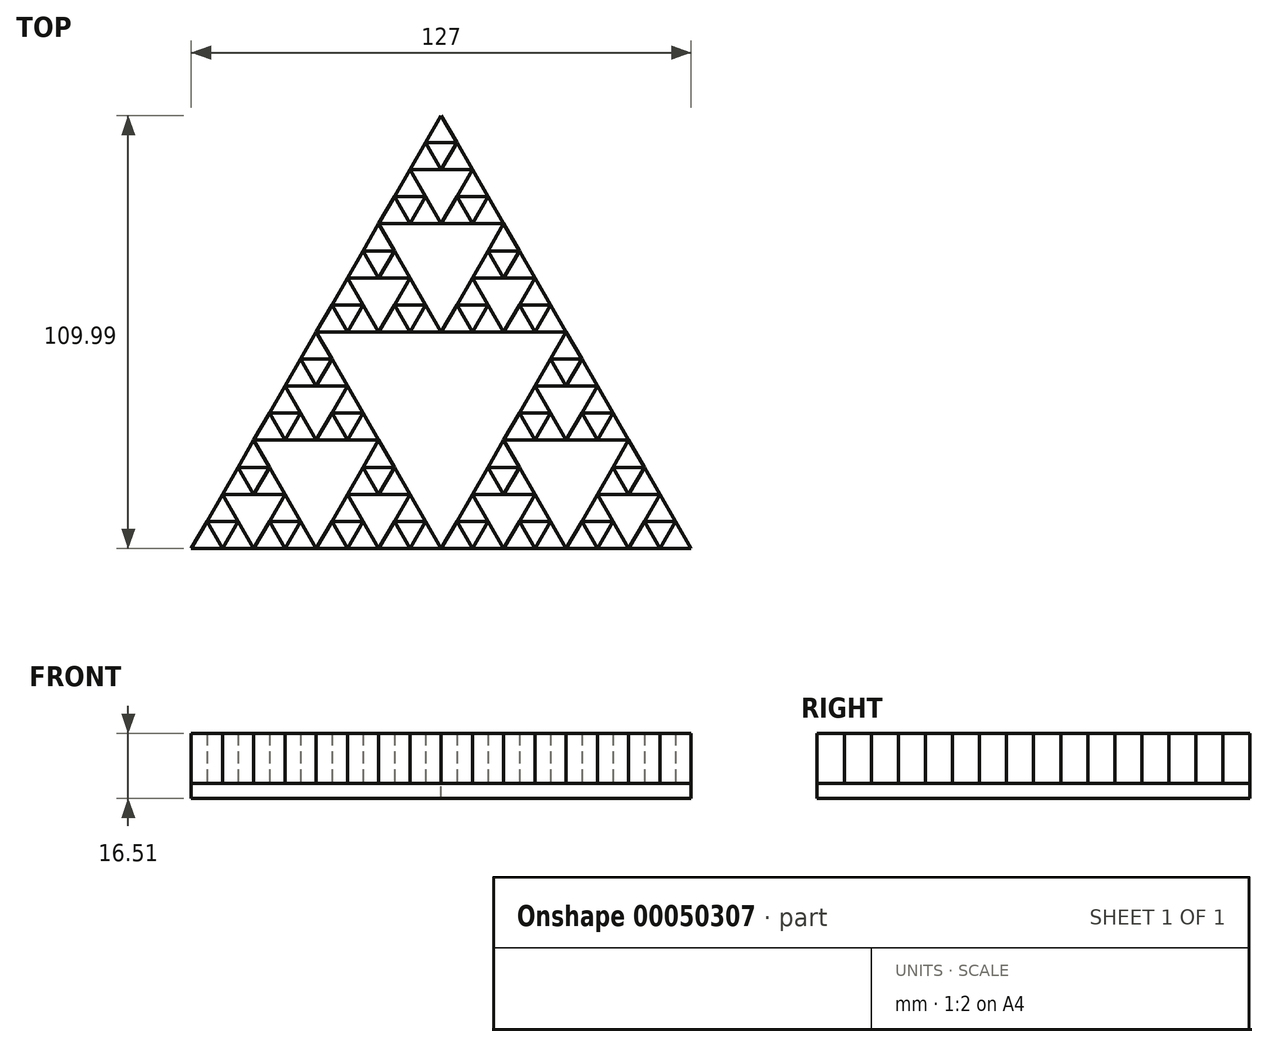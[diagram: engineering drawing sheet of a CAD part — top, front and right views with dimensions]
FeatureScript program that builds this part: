
annotation { "Feature Type Name" : "Feature", "Feature Type Description" : "" }
export const myFeature = defineFeature(function(context is Context, id is Id, definition is map)
    precondition{}
    {
        {
            var Q0;
            Q0=qCreatedBy(makeId("Top.planeOp"),FACE);
            var sketch = newSketch(context, id + "F0", { "sketchPlane" : qUnion([Q0])});
            skLineSegment(sketch, "E0", {"start": v(0, 109.99) * mm, "end": v(-63.5, 0) * mm});
            skLineSegment(sketch, "E1", {"start": v(-63.5, 0) * mm, "end": v(63.5, 0) * mm});
            skLineSegment(sketch, "E2", {"start": v(63.5, 0) * mm, "end": v(0, 109.99) * mm});
            skLineSegment(sketch, "E3", {"start": v(31.75, 55) * mm, "end": v(-31.75, 55) * mm});
            skLineSegment(sketch, "E4", {"start": v(-31.75, 55) * mm, "end": v(0, 0) * mm});
            skLineSegment(sketch, "E5", {"start": v(0, 0) * mm, "end": v(31.75, 55) * mm});
            skLineSegment(sketch, "E6", {"start": v(0, 55) * mm, "end": v(-15.88, 82.49) * mm});
            skLineSegment(sketch, "E7", {"start": v(-15.88, 82.49) * mm, "end": v(15.88, 82.49) * mm});
            skLineSegment(sketch, "E8", {"start": v(15.87, 82.49) * mm, "end": v(0, 55) * mm});
            skLineSegment(sketch, "E9", {"start": v(-15.88, 27.5) * mm, "end": v(-47.63, 27.5) * mm});
            skLineSegment(sketch, "E10", {"start": v(15.87, 27.5) * mm, "end": v(47.62, 27.5) * mm});
            skLineSegment(sketch, "E11", {"start": v(47.62, 27.5) * mm, "end": v(31.75, 0) * mm});
            skLineSegment(sketch, "E12", {"start": v(31.75, 0) * mm, "end": v(15.87, 27.5) * mm});
            skLineSegment(sketch, "E13", {"start": v(-15.88, 27.5) * mm, "end": v(-31.75, 0) * mm});
            skLineSegment(sketch, "E14", {"start": v(-31.75, 0) * mm, "end": v(-47.63, 27.5) * mm});
            skLineSegment(sketch, "E15", {"start": v(-31.75, 27.5) * mm, "end": v(-39.69, 41.24) * mm});
            skLineSegment(sketch, "E16", {"start": v(-39.69, 41.24) * mm, "end": v(-23.81, 41.24) * mm});
            skLineSegment(sketch, "E17", {"start": v(-23.81, 41.24) * mm, "end": v(-31.75, 27.5) * mm});
            skLineSegment(sketch, "E18", {"start": v(-23.81, 13.75) * mm, "end": v(-15.88, 0) * mm});
            skLineSegment(sketch, "E19", {"start": v(-15.88, 0) * mm, "end": v(-7.94, 13.75) * mm});
            skLineSegment(sketch, "E20", {"start": v(-7.94, 13.75) * mm, "end": v(-23.81, 13.75) * mm});
            skLineSegment(sketch, "E21", {"start": v(-39.69, 13.75) * mm, "end": v(-55.56, 13.75) * mm});
            skLineSegment(sketch, "E22", {"start": v(-39.69, 13.75) * mm, "end": v(-47.63, 0) * mm});
            skPoint(sketch, "E22.endSnap0", {"position": v(-47.63, 13.75) * mm});
            skLineSegment(sketch, "E23", {"start": v(-47.63, 0) * mm, "end": v(-55.56, 13.75) * mm});
            skLineSegment(sketch, "E24", {"start": v(23.81, 13.75) * mm, "end": v(15.87, 0) * mm});
            skLineSegment(sketch, "E25", {"start": v(15.87, 0) * mm, "end": v(7.94, 13.75) * mm});
            skLineSegment(sketch, "E26", {"start": v(7.94, 13.75) * mm, "end": v(23.81, 13.75) * mm});
            skLineSegment(sketch, "E27", {"start": v(39.69, 13.75) * mm, "end": v(55.56, 13.75) * mm});
            skLineSegment(sketch, "E28", {"start": v(55.56, 13.75) * mm, "end": v(47.62, 0) * mm});
            skPoint(sketch, "E28.endSnap0", {"position": v(47.62, 13.75) * mm});
            skLineSegment(sketch, "E29", {"start": v(47.62, 0) * mm, "end": v(39.69, 13.75) * mm});
            skLineSegment(sketch, "E30", {"start": v(31.75, 27.5) * mm, "end": v(23.81, 41.24) * mm});
            skLineSegment(sketch, "E31", {"start": v(23.81, 41.24) * mm, "end": v(39.69, 41.24) * mm});
            skLineSegment(sketch, "E32", {"start": v(39.69, 41.24) * mm, "end": v(31.75, 27.5) * mm});
            skLineSegment(sketch, "E33", {"start": v(7.94, 68.74) * mm, "end": v(15.87, 55) * mm});
            skLineSegment(sketch, "E34", {"start": v(15.87, 55) * mm, "end": v(23.81, 68.74) * mm});
            skLineSegment(sketch, "E35", {"start": v(23.81, 68.74) * mm, "end": v(7.94, 68.74) * mm});
            skLineSegment(sketch, "E36", {"start": v(-7.94, 68.74) * mm, "end": v(-15.88, 55) * mm});
            skLineSegment(sketch, "E37", {"start": v(-15.88, 55) * mm, "end": v(-23.81, 68.74) * mm});
            skLineSegment(sketch, "E38", {"start": v(-23.81, 68.74) * mm, "end": v(-7.94, 68.74) * mm});
            skLineSegment(sketch, "E39", {"start": v(0, 82.49) * mm, "end": v(-7.94, 96.24) * mm});
            skLineSegment(sketch, "E40", {"start": v(-7.94, 96.24) * mm, "end": v(7.94, 96.24) * mm});
            skLineSegment(sketch, "E41", {"start": v(7.94, 96.24) * mm, "end": v(0, 82.49) * mm});
            skLineSegment(sketch, "E42", {"start": v(0, 96.24) * mm, "end": v(3.97, 103.11) * mm});
            skLineSegment(sketch, "E43", {"start": v(3.97, 103.11) * mm, "end": v(-3.97, 103.11) * mm});
            skLineSegment(sketch, "E44", {"start": v(-3.97, 103.11) * mm, "end": v(0, 96.24) * mm});
            skLineSegment(sketch, "E45", {"start": v(-3.97, 89.36) * mm, "end": v(-11.9, 89.36) * mm});
            skLineSegment(sketch, "E46", {"start": v(-11.9, 89.36) * mm, "end": v(-7.94, 82.49) * mm});
            skLineSegment(sketch, "E47", {"start": v(-7.94, 82.49) * mm, "end": v(-3.97, 89.36) * mm});
            skLineSegment(sketch, "E48", {"start": v(3.97, 89.36) * mm, "end": v(11.9, 89.36) * mm});
            skLineSegment(sketch, "E49", {"start": v(11.9, 89.36) * mm, "end": v(7.94, 82.49) * mm});
            skLineSegment(sketch, "E50", {"start": v(7.94, 82.49) * mm, "end": v(3.97, 89.36) * mm});
            skLineSegment(sketch, "E51", {"start": v(-15.88, 68.74) * mm, "end": v(-19.84, 75.61) * mm});
            skLineSegment(sketch, "E52", {"start": v(-19.84, 75.61) * mm, "end": v(-11.9, 75.61) * mm});
            skLineSegment(sketch, "E53", {"start": v(-11.9, 75.61) * mm, "end": v(-15.88, 68.74) * mm});
            skLineSegment(sketch, "E54", {"start": v(-19.84, 61.87) * mm, "end": v(-27.78, 61.87) * mm});
            skLineSegment(sketch, "E55", {"start": v(-27.78, 61.87) * mm, "end": v(-23.81, 55) * mm});
            skLineSegment(sketch, "E56", {"start": v(-23.81, 55) * mm, "end": v(-19.84, 61.87) * mm});
            skLineSegment(sketch, "E57", {"start": v(-11.9, 61.87) * mm, "end": v(-3.97, 61.87) * mm});
            skPoint(sketch, "E57.endSnap0", {"position": v(-11.9, 61.87) * mm});
            skLineSegment(sketch, "E58", {"start": v(-3.97, 61.87) * mm, "end": v(-7.94, 55) * mm});
            skLineSegment(sketch, "E59", {"start": v(-7.94, 55) * mm, "end": v(-11.9, 61.87) * mm});
            skLineSegment(sketch, "E60", {"start": v(11.9, 61.87) * mm, "end": v(3.97, 61.87) * mm});
            skPoint(sketch, "E60.endSnap0", {"position": v(11.9, 61.87) * mm});
            skLineSegment(sketch, "E61", {"start": v(3.97, 61.87) * mm, "end": v(7.94, 55) * mm});
            skLineSegment(sketch, "E62", {"start": v(7.94, 55) * mm, "end": v(11.9, 61.87) * mm});
            skLineSegment(sketch, "E63", {"start": v(15.87, 68.74) * mm, "end": v(11.9, 75.61) * mm});
            skLineSegment(sketch, "E64", {"start": v(11.9, 75.61) * mm, "end": v(19.84, 75.61) * mm});
            skLineSegment(sketch, "E65", {"start": v(19.84, 75.61) * mm, "end": v(15.87, 68.74) * mm});
            skLineSegment(sketch, "E66", {"start": v(19.84, 61.87) * mm, "end": v(27.78, 61.87) * mm});
            skLineSegment(sketch, "E67", {"start": v(27.78, 61.87) * mm, "end": v(23.81, 55) * mm});
            skLineSegment(sketch, "E68", {"start": v(23.81, 55) * mm, "end": v(19.84, 61.87) * mm});
            skLineSegment(sketch, "E69", {"start": v(31.75, 41.24) * mm, "end": v(35.72, 48.12) * mm});
            skLineSegment(sketch, "E70", {"start": v(35.72, 48.12) * mm, "end": v(27.78, 48.12) * mm});
            skLineSegment(sketch, "E71", {"start": v(27.78, 48.12) * mm, "end": v(31.75, 41.24) * mm});
            skLineSegment(sketch, "E72", {"start": v(27.78, 34.37) * mm, "end": v(19.84, 34.37) * mm});
            skPoint(sketch, "E72.endSnap0", {"position": v(27.78, 34.37) * mm});
            skLineSegment(sketch, "E73", {"start": v(19.84, 34.37) * mm, "end": v(23.81, 27.5) * mm});
            skLineSegment(sketch, "E74", {"start": v(23.81, 27.5) * mm, "end": v(27.78, 34.37) * mm});
            skLineSegment(sketch, "E75", {"start": v(35.72, 34.37) * mm, "end": v(43.66, 34.37) * mm});
            skPoint(sketch, "E75.endSnap0", {"position": v(35.72, 34.37) * mm});
            skLineSegment(sketch, "E76", {"start": v(43.66, 34.37) * mm, "end": v(39.69, 27.5) * mm});
            skLineSegment(sketch, "E77", {"start": v(39.69, 27.5) * mm, "end": v(35.72, 34.37) * mm});
            skLineSegment(sketch, "E78", {"start": v(15.87, 13.75) * mm, "end": v(11.9, 20.62) * mm});
            skLineSegment(sketch, "E79", {"start": v(11.9, 20.62) * mm, "end": v(19.84, 20.62) * mm});
            skLineSegment(sketch, "E80", {"start": v(19.84, 20.62) * mm, "end": v(15.87, 13.75) * mm});
            skLineSegment(sketch, "E81", {"start": v(47.62, 13.75) * mm, "end": v(51.6, 20.62) * mm});
            skLineSegment(sketch, "E82", {"start": v(19.84, 6.87) * mm, "end": v(27.78, 6.87) * mm});
            skLineSegment(sketch, "E83", {"start": v(27.78, 6.87) * mm, "end": v(23.81, 0) * mm});
            skPoint(sketch, "E83.endSnap0", {"position": v(23.81, 6.87) * mm});
            skLineSegment(sketch, "E84", {"start": v(23.81, 0) * mm, "end": v(19.84, 6.87) * mm});
            skLineSegment(sketch, "E85", {"start": v(11.9, 6.87) * mm, "end": v(3.97, 6.87) * mm});
            skLineSegment(sketch, "E86", {"start": v(3.97, 6.87) * mm, "end": v(7.94, 0) * mm});
            skPoint(sketch, "E86.endSnap0", {"position": v(7.94, 6.87) * mm});
            skLineSegment(sketch, "E87", {"start": v(7.94, 0) * mm, "end": v(11.9, 6.87) * mm});
            skLineSegment(sketch, "E88", {"start": v(47.62, 13.75) * mm, "end": v(43.66, 20.62) * mm});
            skPoint(sketch, "E88.endSnap0", {"position": v(43.66, 6.87) * mm});
            skLineSegment(sketch, "E89", {"start": v(43.66, 20.62) * mm, "end": v(51.6, 20.62) * mm});
            skLineSegment(sketch, "E90", {"start": v(43.66, 6.87) * mm, "end": v(35.72, 6.87) * mm});
            skLineSegment(sketch, "E91", {"start": v(35.72, 6.87) * mm, "end": v(39.69, 0) * mm});
            skPoint(sketch, "E91.endSnap0", {"position": v(39.69, 6.87) * mm});
            skLineSegment(sketch, "E92", {"start": v(39.69, 0) * mm, "end": v(43.66, 6.87) * mm});
            skLineSegment(sketch, "E93", {"start": v(51.6, 6.87) * mm, "end": v(59.53, 6.87) * mm});
            skLineSegment(sketch, "E94", {"start": v(59.53, 6.87) * mm, "end": v(55.56, 0) * mm});
            skPoint(sketch, "E94.endSnap0", {"position": v(55.56, 6.87) * mm});
            skLineSegment(sketch, "E95", {"start": v(55.56, 0) * mm, "end": v(51.6, 6.87) * mm});
            skLineSegment(sketch, "E96", {"start": v(-31.75, 41.24) * mm, "end": v(-35.72, 48.12) * mm});
            skLineSegment(sketch, "E97", {"start": v(-35.72, 48.12) * mm, "end": v(-27.78, 48.12) * mm});
            skLineSegment(sketch, "E98", {"start": v(-27.78, 48.12) * mm, "end": v(-31.75, 41.24) * mm});
            skLineSegment(sketch, "E99", {"start": v(-35.72, 34.37) * mm, "end": v(-43.66, 34.37) * mm});
            skLineSegment(sketch, "E100", {"start": v(-43.66, 34.37) * mm, "end": v(-39.69, 27.5) * mm});
            skLineSegment(sketch, "E101", {"start": v(-39.69, 27.5) * mm, "end": v(-35.72, 34.37) * mm});
            skLineSegment(sketch, "E102", {"start": v(-27.78, 34.37) * mm, "end": v(-19.84, 34.37) * mm});
            skLineSegment(sketch, "E103", {"start": v(-19.84, 34.37) * mm, "end": v(-23.81, 27.5) * mm});
            skLineSegment(sketch, "E104", {"start": v(-23.81, 27.5) * mm, "end": v(-27.78, 34.37) * mm});
            skLineSegment(sketch, "E105", {"start": v(-47.63, 13.75) * mm, "end": v(-51.6, 20.62) * mm});
            skLineSegment(sketch, "E106", {"start": v(-51.6, 20.62) * mm, "end": v(-43.66, 20.62) * mm});
            skLineSegment(sketch, "E107", {"start": v(-43.66, 20.62) * mm, "end": v(-47.63, 13.75) * mm});
            skLineSegment(sketch, "E108", {"start": v(-15.88, 13.75) * mm, "end": v(-19.84, 20.62) * mm});
            skLineSegment(sketch, "E109", {"start": v(-19.84, 20.62) * mm, "end": v(-11.9, 20.62) * mm});
            skLineSegment(sketch, "E110", {"start": v(-11.9, 20.62) * mm, "end": v(-15.88, 13.75) * mm});
            skLineSegment(sketch, "E111", {"start": v(-19.84, 6.87) * mm, "end": v(-27.78, 6.87) * mm});
            skPoint(sketch, "E111.endSnap0", {"position": v(-19.84, 6.87) * mm});
            skLineSegment(sketch, "E112", {"start": v(-27.78, 6.87) * mm, "end": v(-23.81, 0) * mm});
            skPoint(sketch, "E112.endSnap0", {"position": v(-23.81, 6.87) * mm});
            skLineSegment(sketch, "E113", {"start": v(-23.81, 0) * mm, "end": v(-19.84, 6.87) * mm});
            skLineSegment(sketch, "E114", {"start": v(-43.66, 6.87) * mm, "end": v(-35.72, 6.87) * mm});
            skLineSegment(sketch, "E115", {"start": v(-35.72, 6.87) * mm, "end": v(-39.69, 0) * mm});
            skPoint(sketch, "E115.endSnap0", {"position": v(-39.69, 6.87) * mm});
            skLineSegment(sketch, "E116", {"start": v(-39.69, 0) * mm, "end": v(-43.66, 6.87) * mm});
            skLineSegment(sketch, "E117", {"start": v(-3.97, 6.87) * mm, "end": v(-11.9, 6.87) * mm});
            skPoint(sketch, "E117.startSnap0", {"position": v(-11.9, 6.87) * mm});
            skLineSegment(sketch, "E118", {"start": v(-11.9, 6.87) * mm, "end": v(-7.94, 0) * mm});
            skPoint(sketch, "E118.endSnap0", {"position": v(-7.94, 6.87) * mm});
            skLineSegment(sketch, "E119", {"start": v(-7.94, 0) * mm, "end": v(-3.97, 6.87) * mm});
            skLineSegment(sketch, "E120", {"start": v(-51.6, 6.87) * mm, "end": v(-59.53, 6.87) * mm});
            skLineSegment(sketch, "E121", {"start": v(-59.53, 6.87) * mm, "end": v(-55.56, 0) * mm});
            skPoint(sketch, "E121.endSnap0", {"position": v(-55.56, 6.87) * mm});
            skLineSegment(sketch, "E122", {"start": v(-55.56, 0) * mm, "end": v(-51.6, 6.87) * mm});
            skSolve(sketch);
        }
        {
            var Q0;
            {var subQ3=sQuery(id+"F0.wireOp",EDGE,"E43");Q0=makeQuery(id+"F0.imprint","IMPRINT",FACE,{"disambiguationData":[TD([[makeQuery(id+"F0.imprint","IMPRINT",EDGE,{"derivedFrom":subQ3}),-1.0]])]});}
            var Q1;
            {var subQ3=sQuery(id+"F0.wireOp",EDGE,"E44");Q1=makeQuery(id+"F0.imprint","IMPRINT",FACE,{"disambiguationData":[TD([[makeQuery(id+"F0.imprint","IMPRINT",EDGE,{"derivedFrom":subQ3}),-1.0]])]});}
            var Q2;
            {var subQ3=sQuery(id+"F0.wireOp",EDGE,"E42");Q2=makeQuery(id+"F0.imprint","IMPRINT",FACE,{"disambiguationData":[TD([[makeQuery(id+"F0.imprint","IMPRINT",EDGE,{"derivedFrom":subQ3}),-1.0]])]});}
            var Q3;
            {var subQ3=sQuery(id+"F0.wireOp",EDGE,"E48");Q3=makeQuery(id+"F0.imprint","IMPRINT",FACE,{"disambiguationData":[TD([[makeQuery(id+"F0.imprint","IMPRINT",EDGE,{"derivedFrom":subQ3}),1.0]])]});}
            var Q4;
            {var subQ3=sQuery(id+"F0.wireOp",EDGE,"E49");Q4=makeQuery(id+"F0.imprint","IMPRINT",FACE,{"disambiguationData":[TD([[makeQuery(id+"F0.imprint","IMPRINT",EDGE,{"derivedFrom":subQ3}),1.0]])]});}
            var Q5;
            {var subQ3=sQuery(id+"F0.wireOp",EDGE,"E50");Q5=makeQuery(id+"F0.imprint","IMPRINT",FACE,{"disambiguationData":[TD([[makeQuery(id+"F0.imprint","IMPRINT",EDGE,{"derivedFrom":subQ3}),1.0]])]});}
            var Q6;
            {var subQ3=sQuery(id+"F0.wireOp",EDGE,"E47");Q6=makeQuery(id+"F0.imprint","IMPRINT",FACE,{"disambiguationData":[TD([[makeQuery(id+"F0.imprint","IMPRINT",EDGE,{"derivedFrom":subQ3}),-1.0]])]});}
            var Q7;
            {var subQ3=sQuery(id+"F0.wireOp",EDGE,"E45");Q7=makeQuery(id+"F0.imprint","IMPRINT",FACE,{"disambiguationData":[TD([[makeQuery(id+"F0.imprint","IMPRINT",EDGE,{"derivedFrom":subQ3}),-1.0]])]});}
            var Q8;
            {var subQ3=sQuery(id+"F0.wireOp",EDGE,"E46");Q8=makeQuery(id+"F0.imprint","IMPRINT",FACE,{"disambiguationData":[TD([[makeQuery(id+"F0.imprint","IMPRINT",EDGE,{"derivedFrom":subQ3}),-1.0]])]});}
            var Q9;
            {var subQ3=sQuery(id+"F0.wireOp",EDGE,"E52");Q9=makeQuery(id+"F0.imprint","IMPRINT",FACE,{"disambiguationData":[TD([[makeQuery(id+"F0.imprint","IMPRINT",EDGE,{"derivedFrom":subQ3}),1.0]])]});}
            var Q10;
            {var subQ3=sQuery(id+"F0.wireOp",EDGE,"E51");Q10=makeQuery(id+"F0.imprint","IMPRINT",FACE,{"disambiguationData":[TD([[makeQuery(id+"F0.imprint","IMPRINT",EDGE,{"derivedFrom":subQ3}),1.0]])]});}
            var Q11;
            {var subQ3=sQuery(id+"F0.wireOp",EDGE,"E53");Q11=makeQuery(id+"F0.imprint","IMPRINT",FACE,{"disambiguationData":[TD([[makeQuery(id+"F0.imprint","IMPRINT",EDGE,{"derivedFrom":subQ3}),1.0]])]});}
            var Q12;
            {var subQ3=sQuery(id+"F0.wireOp",EDGE,"E64");Q12=makeQuery(id+"F0.imprint","IMPRINT",FACE,{"disambiguationData":[TD([[makeQuery(id+"F0.imprint","IMPRINT",EDGE,{"derivedFrom":subQ3}),1.0]])]});}
            var Q13;
            {var subQ3=sQuery(id+"F0.wireOp",EDGE,"E65");Q13=makeQuery(id+"F0.imprint","IMPRINT",FACE,{"disambiguationData":[TD([[makeQuery(id+"F0.imprint","IMPRINT",EDGE,{"derivedFrom":subQ3}),1.0]])]});}
            var Q14;
            {var subQ3=sQuery(id+"F0.wireOp",EDGE,"E63");Q14=makeQuery(id+"F0.imprint","IMPRINT",FACE,{"disambiguationData":[TD([[makeQuery(id+"F0.imprint","IMPRINT",EDGE,{"derivedFrom":subQ3}),1.0]])]});}
            var Q15;
            {var subQ3=sQuery(id+"F0.wireOp",EDGE,"E60");Q15=makeQuery(id+"F0.imprint","IMPRINT",FACE,{"disambiguationData":[TD([[makeQuery(id+"F0.imprint","IMPRINT",EDGE,{"derivedFrom":subQ3}),-1.0]])]});}
            var Q16;
            {var subQ3=sQuery(id+"F0.wireOp",EDGE,"E62");Q16=makeQuery(id+"F0.imprint","IMPRINT",FACE,{"disambiguationData":[TD([[makeQuery(id+"F0.imprint","IMPRINT",EDGE,{"derivedFrom":subQ3}),-1.0]])]});}
            var Q17;
            {var subQ3=sQuery(id+"F0.wireOp",EDGE,"E61");Q17=makeQuery(id+"F0.imprint","IMPRINT",FACE,{"disambiguationData":[TD([[makeQuery(id+"F0.imprint","IMPRINT",EDGE,{"derivedFrom":subQ3}),-1.0]])]});}
            var Q18;
            {var subQ3=sQuery(id+"F0.wireOp",EDGE,"E57");Q18=makeQuery(id+"F0.imprint","IMPRINT",FACE,{"disambiguationData":[TD([[makeQuery(id+"F0.imprint","IMPRINT",EDGE,{"derivedFrom":subQ3}),1.0]])]});}
            var Q19;
            {var subQ3=sQuery(id+"F0.wireOp",EDGE,"E58");Q19=makeQuery(id+"F0.imprint","IMPRINT",FACE,{"disambiguationData":[TD([[makeQuery(id+"F0.imprint","IMPRINT",EDGE,{"derivedFrom":subQ3}),1.0]])]});}
            var Q20;
            {var subQ3=sQuery(id+"F0.wireOp",EDGE,"E59");Q20=makeQuery(id+"F0.imprint","IMPRINT",FACE,{"disambiguationData":[TD([[makeQuery(id+"F0.imprint","IMPRINT",EDGE,{"derivedFrom":subQ3}),1.0]])]});}
            var Q21;
            {var subQ3=sQuery(id+"F0.wireOp",EDGE,"E56");Q21=makeQuery(id+"F0.imprint","IMPRINT",FACE,{"disambiguationData":[TD([[makeQuery(id+"F0.imprint","IMPRINT",EDGE,{"derivedFrom":subQ3}),-1.0]])]});}
            var Q22;
            {var subQ3=sQuery(id+"F0.wireOp",EDGE,"E54");Q22=makeQuery(id+"F0.imprint","IMPRINT",FACE,{"disambiguationData":[TD([[makeQuery(id+"F0.imprint","IMPRINT",EDGE,{"derivedFrom":subQ3}),-1.0]])]});}
            var Q23;
            {var subQ3=sQuery(id+"F0.wireOp",EDGE,"E55");Q23=makeQuery(id+"F0.imprint","IMPRINT",FACE,{"disambiguationData":[TD([[makeQuery(id+"F0.imprint","IMPRINT",EDGE,{"derivedFrom":subQ3}),-1.0]])]});}
            var Q24;
            {var subQ3=sQuery(id+"F0.wireOp",EDGE,"E66");Q24=makeQuery(id+"F0.imprint","IMPRINT",FACE,{"disambiguationData":[TD([[makeQuery(id+"F0.imprint","IMPRINT",EDGE,{"derivedFrom":subQ3}),1.0]])]});}
            var Q25;
            {var subQ3=sQuery(id+"F0.wireOp",EDGE,"E67");Q25=makeQuery(id+"F0.imprint","IMPRINT",FACE,{"disambiguationData":[TD([[makeQuery(id+"F0.imprint","IMPRINT",EDGE,{"derivedFrom":subQ3}),1.0]])]});}
            var Q26;
            {var subQ3=sQuery(id+"F0.wireOp",EDGE,"E68");Q26=makeQuery(id+"F0.imprint","IMPRINT",FACE,{"disambiguationData":[TD([[makeQuery(id+"F0.imprint","IMPRINT",EDGE,{"derivedFrom":subQ3}),1.0]])]});}
            var Q27;
            {var subQ3=sQuery(id+"F0.wireOp",EDGE,"E97");Q27=makeQuery(id+"F0.imprint","IMPRINT",FACE,{"disambiguationData":[TD([[makeQuery(id+"F0.imprint","IMPRINT",EDGE,{"derivedFrom":subQ3}),1.0]])]});}
            var Q28;
            {var subQ3=sQuery(id+"F0.wireOp",EDGE,"E96");Q28=makeQuery(id+"F0.imprint","IMPRINT",FACE,{"disambiguationData":[TD([[makeQuery(id+"F0.imprint","IMPRINT",EDGE,{"derivedFrom":subQ3}),1.0]])]});}
            var Q29;
            {var subQ3=sQuery(id+"F0.wireOp",EDGE,"E98");Q29=makeQuery(id+"F0.imprint","IMPRINT",FACE,{"disambiguationData":[TD([[makeQuery(id+"F0.imprint","IMPRINT",EDGE,{"derivedFrom":subQ3}),1.0]])]});}
            var Q30;
            {var subQ3=sQuery(id+"F0.wireOp",EDGE,"E102");Q30=makeQuery(id+"F0.imprint","IMPRINT",FACE,{"disambiguationData":[TD([[makeQuery(id+"F0.imprint","IMPRINT",EDGE,{"derivedFrom":subQ3}),1.0]])]});}
            var Q31;
            {var subQ3=sQuery(id+"F0.wireOp",EDGE,"E104");Q31=makeQuery(id+"F0.imprint","IMPRINT",FACE,{"disambiguationData":[TD([[makeQuery(id+"F0.imprint","IMPRINT",EDGE,{"derivedFrom":subQ3}),1.0]])]});}
            var Q32;
            {var subQ3=sQuery(id+"F0.wireOp",EDGE,"E103");Q32=makeQuery(id+"F0.imprint","IMPRINT",FACE,{"disambiguationData":[TD([[makeQuery(id+"F0.imprint","IMPRINT",EDGE,{"derivedFrom":subQ3}),1.0]])]});}
            var Q33;
            {var subQ3=sQuery(id+"F0.wireOp",EDGE,"E100");Q33=makeQuery(id+"F0.imprint","IMPRINT",FACE,{"disambiguationData":[TD([[makeQuery(id+"F0.imprint","IMPRINT",EDGE,{"derivedFrom":subQ3}),-1.0]])]});}
            var Q34;
            {var subQ3=sQuery(id+"F0.wireOp",EDGE,"E101");Q34=makeQuery(id+"F0.imprint","IMPRINT",FACE,{"disambiguationData":[TD([[makeQuery(id+"F0.imprint","IMPRINT",EDGE,{"derivedFrom":subQ3}),-1.0]])]});}
            var Q35;
            {var subQ3=sQuery(id+"F0.wireOp",EDGE,"E99");Q35=makeQuery(id+"F0.imprint","IMPRINT",FACE,{"disambiguationData":[TD([[makeQuery(id+"F0.imprint","IMPRINT",EDGE,{"derivedFrom":subQ3}),-1.0]])]});}
            var Q36;
            {var subQ3=sQuery(id+"F0.wireOp",EDGE,"E106");Q36=makeQuery(id+"F0.imprint","IMPRINT",FACE,{"disambiguationData":[TD([[makeQuery(id+"F0.imprint","IMPRINT",EDGE,{"derivedFrom":subQ3}),1.0]])]});}
            var Q37;
            {var subQ3=sQuery(id+"F0.wireOp",EDGE,"E105");Q37=makeQuery(id+"F0.imprint","IMPRINT",FACE,{"disambiguationData":[TD([[makeQuery(id+"F0.imprint","IMPRINT",EDGE,{"derivedFrom":subQ3}),1.0]])]});}
            var Q38;
            {var subQ3=sQuery(id+"F0.wireOp",EDGE,"E107");Q38=makeQuery(id+"F0.imprint","IMPRINT",FACE,{"disambiguationData":[TD([[makeQuery(id+"F0.imprint","IMPRINT",EDGE,{"derivedFrom":subQ3}),1.0]])]});}
            var Q39;
            {var subQ3=sQuery(id+"F0.wireOp",EDGE,"E114");Q39=makeQuery(id+"F0.imprint","IMPRINT",FACE,{"disambiguationData":[TD([[makeQuery(id+"F0.imprint","IMPRINT",EDGE,{"derivedFrom":subQ3}),1.0]])]});}
            var Q40;
            {var subQ3=sQuery(id+"F0.wireOp",EDGE,"E115");Q40=makeQuery(id+"F0.imprint","IMPRINT",FACE,{"disambiguationData":[TD([[makeQuery(id+"F0.imprint","IMPRINT",EDGE,{"derivedFrom":subQ3}),1.0]])]});}
            var Q41;
            {var subQ3=sQuery(id+"F0.wireOp",EDGE,"E116");Q41=makeQuery(id+"F0.imprint","IMPRINT",FACE,{"disambiguationData":[TD([[makeQuery(id+"F0.imprint","IMPRINT",EDGE,{"derivedFrom":subQ3}),1.0]])]});}
            var Q42;
            {var subQ3=sQuery(id+"F0.wireOp",EDGE,"E122");Q42=makeQuery(id+"F0.imprint","IMPRINT",FACE,{"disambiguationData":[TD([[makeQuery(id+"F0.imprint","IMPRINT",EDGE,{"derivedFrom":subQ3}),-1.0]])]});}
            var Q43;
            {var subQ3=sQuery(id+"F0.wireOp",EDGE,"E120");Q43=makeQuery(id+"F0.imprint","IMPRINT",FACE,{"disambiguationData":[TD([[makeQuery(id+"F0.imprint","IMPRINT",EDGE,{"derivedFrom":subQ3}),-1.0]])]});}
            var Q44;
            {var subQ3=sQuery(id+"F0.wireOp",EDGE,"E121");Q44=makeQuery(id+"F0.imprint","IMPRINT",FACE,{"disambiguationData":[TD([[makeQuery(id+"F0.imprint","IMPRINT",EDGE,{"derivedFrom":subQ3}),-1.0]])]});}
            var Q45;
            {var subQ3=sQuery(id+"F0.wireOp",EDGE,"E110");Q45=makeQuery(id+"F0.imprint","IMPRINT",FACE,{"disambiguationData":[TD([[makeQuery(id+"F0.imprint","IMPRINT",EDGE,{"derivedFrom":subQ3}),1.0]])]});}
            var Q46;
            {var subQ3=sQuery(id+"F0.wireOp",EDGE,"E108");Q46=makeQuery(id+"F0.imprint","IMPRINT",FACE,{"disambiguationData":[TD([[makeQuery(id+"F0.imprint","IMPRINT",EDGE,{"derivedFrom":subQ3}),1.0]])]});}
            var Q47;
            {var subQ3=sQuery(id+"F0.wireOp",EDGE,"E109");Q47=makeQuery(id+"F0.imprint","IMPRINT",FACE,{"disambiguationData":[TD([[makeQuery(id+"F0.imprint","IMPRINT",EDGE,{"derivedFrom":subQ3}),1.0]])]});}
            var Q48;
            {var subQ3=sQuery(id+"F0.wireOp",EDGE,"E117");Q48=makeQuery(id+"F0.imprint","IMPRINT",FACE,{"disambiguationData":[TD([[makeQuery(id+"F0.imprint","IMPRINT",EDGE,{"derivedFrom":subQ3}),-1.0]])]});}
            var Q49;
            {var subQ3=sQuery(id+"F0.wireOp",EDGE,"E119");Q49=makeQuery(id+"F0.imprint","IMPRINT",FACE,{"disambiguationData":[TD([[makeQuery(id+"F0.imprint","IMPRINT",EDGE,{"derivedFrom":subQ3}),-1.0]])]});}
            var Q50;
            {var subQ3=sQuery(id+"F0.wireOp",EDGE,"E118");Q50=makeQuery(id+"F0.imprint","IMPRINT",FACE,{"disambiguationData":[TD([[makeQuery(id+"F0.imprint","IMPRINT",EDGE,{"derivedFrom":subQ3}),-1.0]])]});}
            var Q51;
            {var subQ3=sQuery(id+"F0.wireOp",EDGE,"E113");Q51=makeQuery(id+"F0.imprint","IMPRINT",FACE,{"disambiguationData":[TD([[makeQuery(id+"F0.imprint","IMPRINT",EDGE,{"derivedFrom":subQ3}),-1.0]])]});}
            var Q52;
            {var subQ3=sQuery(id+"F0.wireOp",EDGE,"E111");Q52=makeQuery(id+"F0.imprint","IMPRINT",FACE,{"disambiguationData":[TD([[makeQuery(id+"F0.imprint","IMPRINT",EDGE,{"derivedFrom":subQ3}),-1.0]])]});}
            var Q53;
            {var subQ3=sQuery(id+"F0.wireOp",EDGE,"E112");Q53=makeQuery(id+"F0.imprint","IMPRINT",FACE,{"disambiguationData":[TD([[makeQuery(id+"F0.imprint","IMPRINT",EDGE,{"derivedFrom":subQ3}),-1.0]])]});}
            var Q54;
            {var subQ3=sQuery(id+"F0.wireOp",EDGE,"E70");Q54=makeQuery(id+"F0.imprint","IMPRINT",FACE,{"disambiguationData":[TD([[makeQuery(id+"F0.imprint","IMPRINT",EDGE,{"derivedFrom":subQ3}),-1.0]])]});}
            var Q55;
            {var subQ3=sQuery(id+"F0.wireOp",EDGE,"E69");Q55=makeQuery(id+"F0.imprint","IMPRINT",FACE,{"disambiguationData":[TD([[makeQuery(id+"F0.imprint","IMPRINT",EDGE,{"derivedFrom":subQ3}),-1.0]])]});}
            var Q56;
            {var subQ3=sQuery(id+"F0.wireOp",EDGE,"E71");Q56=makeQuery(id+"F0.imprint","IMPRINT",FACE,{"disambiguationData":[TD([[makeQuery(id+"F0.imprint","IMPRINT",EDGE,{"derivedFrom":subQ3}),-1.0]])]});}
            var Q57;
            {var subQ3=sQuery(id+"F0.wireOp",EDGE,"E72");Q57=makeQuery(id+"F0.imprint","IMPRINT",FACE,{"disambiguationData":[TD([[makeQuery(id+"F0.imprint","IMPRINT",EDGE,{"derivedFrom":subQ3}),-1.0]])]});}
            var Q58;
            {var subQ3=sQuery(id+"F0.wireOp",EDGE,"E74");Q58=makeQuery(id+"F0.imprint","IMPRINT",FACE,{"disambiguationData":[TD([[makeQuery(id+"F0.imprint","IMPRINT",EDGE,{"derivedFrom":subQ3}),-1.0]])]});}
            var Q59;
            {var subQ3=sQuery(id+"F0.wireOp",EDGE,"E73");Q59=makeQuery(id+"F0.imprint","IMPRINT",FACE,{"disambiguationData":[TD([[makeQuery(id+"F0.imprint","IMPRINT",EDGE,{"derivedFrom":subQ3}),-1.0]])]});}
            var Q60;
            {var subQ3=sQuery(id+"F0.wireOp",EDGE,"E79");Q60=makeQuery(id+"F0.imprint","IMPRINT",FACE,{"disambiguationData":[TD([[makeQuery(id+"F0.imprint","IMPRINT",EDGE,{"derivedFrom":subQ3}),1.0]])]});}
            var Q61;
            {var subQ3=sQuery(id+"F0.wireOp",EDGE,"E80");Q61=makeQuery(id+"F0.imprint","IMPRINT",FACE,{"disambiguationData":[TD([[makeQuery(id+"F0.imprint","IMPRINT",EDGE,{"derivedFrom":subQ3}),1.0]])]});}
            var Q62;
            {var subQ3=sQuery(id+"F0.wireOp",EDGE,"E78");Q62=makeQuery(id+"F0.imprint","IMPRINT",FACE,{"disambiguationData":[TD([[makeQuery(id+"F0.imprint","IMPRINT",EDGE,{"derivedFrom":subQ3}),1.0]])]});}
            var Q63;
            {var subQ3=sQuery(id+"F0.wireOp",EDGE,"E85");Q63=makeQuery(id+"F0.imprint","IMPRINT",FACE,{"disambiguationData":[TD([[makeQuery(id+"F0.imprint","IMPRINT",EDGE,{"derivedFrom":subQ3}),-1.0]])]});}
            var Q64;
            {var subQ3=sQuery(id+"F0.wireOp",EDGE,"E86");Q64=makeQuery(id+"F0.imprint","IMPRINT",FACE,{"disambiguationData":[TD([[makeQuery(id+"F0.imprint","IMPRINT",EDGE,{"derivedFrom":subQ3}),-1.0]])]});}
            var Q65;
            {var subQ3=sQuery(id+"F0.wireOp",EDGE,"E87");Q65=makeQuery(id+"F0.imprint","IMPRINT",FACE,{"disambiguationData":[TD([[makeQuery(id+"F0.imprint","IMPRINT",EDGE,{"derivedFrom":subQ3}),-1.0]])]});}
            var Q66;
            {var subQ3=sQuery(id+"F0.wireOp",EDGE,"E77");Q66=makeQuery(id+"F0.imprint","IMPRINT",FACE,{"disambiguationData":[TD([[makeQuery(id+"F0.imprint","IMPRINT",EDGE,{"derivedFrom":subQ3}),1.0]])]});}
            var Q67;
            {var subQ3=sQuery(id+"F0.wireOp",EDGE,"E75");Q67=makeQuery(id+"F0.imprint","IMPRINT",FACE,{"disambiguationData":[TD([[makeQuery(id+"F0.imprint","IMPRINT",EDGE,{"derivedFrom":subQ3}),1.0]])]});}
            var Q68;
            {var subQ3=sQuery(id+"F0.wireOp",EDGE,"E76");Q68=makeQuery(id+"F0.imprint","IMPRINT",FACE,{"disambiguationData":[TD([[makeQuery(id+"F0.imprint","IMPRINT",EDGE,{"derivedFrom":subQ3}),1.0]])]});}
            var Q69;
            {var subQ3=sQuery(id+"F0.wireOp",EDGE,"E89");Q69=makeQuery(id+"F0.imprint","IMPRINT",FACE,{"disambiguationData":[TD([[makeQuery(id+"F0.imprint","IMPRINT",EDGE,{"derivedFrom":subQ3}),1.0]])]});}
            var Q70;
            {var subQ3=sQuery(id+"F0.wireOp",EDGE,"E88");Q70=makeQuery(id+"F0.imprint","IMPRINT",FACE,{"disambiguationData":[TD([[makeQuery(id+"F0.imprint","IMPRINT",EDGE,{"derivedFrom":subQ3}),1.0]])]});}
            var Q71;
            {var subQ3=sQuery(id+"F0.wireOp",EDGE,"E81");Q71=makeQuery(id+"F0.imprint","IMPRINT",FACE,{"disambiguationData":[TD([[makeQuery(id+"F0.imprint","IMPRINT",EDGE,{"derivedFrom":subQ3}),-1.0]])]});}
            var Q72;
            {var subQ3=sQuery(id+"F0.wireOp",EDGE,"E93");Q72=makeQuery(id+"F0.imprint","IMPRINT",FACE,{"disambiguationData":[TD([[makeQuery(id+"F0.imprint","IMPRINT",EDGE,{"derivedFrom":subQ3}),1.0]])]});}
            var Q73;
            {var subQ3=sQuery(id+"F0.wireOp",EDGE,"E94");Q73=makeQuery(id+"F0.imprint","IMPRINT",FACE,{"disambiguationData":[TD([[makeQuery(id+"F0.imprint","IMPRINT",EDGE,{"derivedFrom":subQ3}),1.0]])]});}
            var Q74;
            {var subQ3=sQuery(id+"F0.wireOp",EDGE,"E95");Q74=makeQuery(id+"F0.imprint","IMPRINT",FACE,{"disambiguationData":[TD([[makeQuery(id+"F0.imprint","IMPRINT",EDGE,{"derivedFrom":subQ3}),1.0]])]});}
            var Q75;
            {var subQ3=sQuery(id+"F0.wireOp",EDGE,"E92");Q75=makeQuery(id+"F0.imprint","IMPRINT",FACE,{"disambiguationData":[TD([[makeQuery(id+"F0.imprint","IMPRINT",EDGE,{"derivedFrom":subQ3}),-1.0]])]});}
            var Q76;
            {var subQ3=sQuery(id+"F0.wireOp",EDGE,"E90");Q76=makeQuery(id+"F0.imprint","IMPRINT",FACE,{"disambiguationData":[TD([[makeQuery(id+"F0.imprint","IMPRINT",EDGE,{"derivedFrom":subQ3}),-1.0]])]});}
            var Q77;
            {var subQ3=sQuery(id+"F0.wireOp",EDGE,"E91");Q77=makeQuery(id+"F0.imprint","IMPRINT",FACE,{"disambiguationData":[TD([[makeQuery(id+"F0.imprint","IMPRINT",EDGE,{"derivedFrom":subQ3}),-1.0]])]});}
            var Q78;
            {var subQ3=sQuery(id+"F0.wireOp",EDGE,"E83");Q78=makeQuery(id+"F0.imprint","IMPRINT",FACE,{"disambiguationData":[TD([[makeQuery(id+"F0.imprint","IMPRINT",EDGE,{"derivedFrom":subQ3}),1.0]])]});}
            var Q79;
            {var subQ3=sQuery(id+"F0.wireOp",EDGE,"E82");Q79=makeQuery(id+"F0.imprint","IMPRINT",FACE,{"disambiguationData":[TD([[makeQuery(id+"F0.imprint","IMPRINT",EDGE,{"derivedFrom":subQ3}),1.0]])]});}
            var Q80;
            {var subQ3=sQuery(id+"F0.wireOp",EDGE,"E84");Q80=makeQuery(id+"F0.imprint","IMPRINT",FACE,{"disambiguationData":[TD([[makeQuery(id+"F0.imprint","IMPRINT",EDGE,{"derivedFrom":subQ3}),1.0]])]});}
            extrude(context, id + "F1", {"entities" : qUnion([Q0, Q1, Q2, Q3, Q4, Q5, Q6, Q7, Q8, Q9, Q10, Q11, Q12, Q13, Q14, Q15, Q16, Q17, Q18, Q19, Q20, Q21, Q22, Q23, Q24, Q25, Q26, Q27, Q28, Q29, Q30, Q31, Q32, Q33, Q34, Q35, Q36, Q37, Q38, Q39, Q40, Q41, Q42, Q43, Q44, Q45, Q46, Q47, Q48, Q49, Q50, Q51, Q52, Q53, Q54, Q55, Q56, Q57, Q58, Q59, Q60, Q61, Q62, Q63, Q64, Q65, Q66, Q67, Q68, Q69, Q70, Q71, Q72, Q73, Q74, Q75, Q76, Q77, Q78, Q79, Q80]), "depth" : 12.7 * mm});
        }
        {
            var Q0;
            {var subQ3=sQuery(id+"F0.wireOp",EDGE,"E43");Q0=makeQuery(id+"F0.imprint","IMPRINT",FACE,{"disambiguationData":[TD([[makeQuery(id+"F0.imprint","IMPRINT",EDGE,{"derivedFrom":subQ3}),-1.0]])]});}
            var Q1;
            Q1=makeQuery(id+"F0.imprint","IMPRINT",FACE,{"disambiguationData":[TD([[makeQuery(id+"F0.imprint","IMPRINT",EDGE,{"derivedFrom":sQuery(id+"F0.wireOp",EDGE,"E42")}),1.0]])]});
            var Q2;
            {var subQ3=sQuery(id+"F0.wireOp",EDGE,"E42");Q2=makeQuery(id+"F0.imprint","IMPRINT",FACE,{"disambiguationData":[TD([[makeQuery(id+"F0.imprint","IMPRINT",EDGE,{"derivedFrom":subQ3}),-1.0]])]});}
            var Q3;
            {var subQ3=sQuery(id+"F0.wireOp",EDGE,"E44");Q3=makeQuery(id+"F0.imprint","IMPRINT",FACE,{"disambiguationData":[TD([[makeQuery(id+"F0.imprint","IMPRINT",EDGE,{"derivedFrom":subQ3}),-1.0]])]});}
            var Q4;
            {var subQ3=sQuery(id+"F0.wireOp",EDGE,"E48");Q4=makeQuery(id+"F0.imprint","IMPRINT",FACE,{"disambiguationData":[TD([[makeQuery(id+"F0.imprint","IMPRINT",EDGE,{"derivedFrom":subQ3}),1.0]])]});}
            var Q5;
            {var subQ0=sQuery(id+"F0.wireOp",EDGE,"E41");var subQ4=sQuery(id+"F0.wireOp",EDGE,"E39");var subQ7=makeQuery(id+"F0.imprint","INTERSECT",VERTEX,{"derivedFrom":[sQuery(id+"F0.wireOp",EDGE,"E7"),subQ4,subQ0]});Q5=makeQuery(id+"F0.imprint","IMPRINT",FACE,{"disambiguationData":[TD([[makeQuery(id+"F0.imprint","IMPRINT",EDGE,{"disambiguationData":[TD([[subQ7,-1.0]])],"derivedFrom":subQ4}),-1.0]])]});}
            var Q6;
            Q6=makeQuery(id+"F0.imprint","IMPRINT",FACE,{"disambiguationData":[TD([[makeQuery(id+"F0.imprint","IMPRINT",EDGE,{"derivedFrom":sQuery(id+"F0.wireOp",EDGE,"E48")}),-1.0]])]});
            var Q7;
            {var subQ3=sQuery(id+"F0.wireOp",EDGE,"E49");Q7=makeQuery(id+"F0.imprint","IMPRINT",FACE,{"disambiguationData":[TD([[makeQuery(id+"F0.imprint","IMPRINT",EDGE,{"derivedFrom":subQ3}),1.0]])]});}
            var Q8;
            {var subQ3=sQuery(id+"F0.wireOp",EDGE,"E50");Q8=makeQuery(id+"F0.imprint","IMPRINT",FACE,{"disambiguationData":[TD([[makeQuery(id+"F0.imprint","IMPRINT",EDGE,{"derivedFrom":subQ3}),1.0]])]});}
            var Q9;
            {var subQ3=sQuery(id+"F0.wireOp",EDGE,"E47");Q9=makeQuery(id+"F0.imprint","IMPRINT",FACE,{"disambiguationData":[TD([[makeQuery(id+"F0.imprint","IMPRINT",EDGE,{"derivedFrom":subQ3}),-1.0]])]});}
            var Q10;
            {var subQ3=sQuery(id+"F0.wireOp",EDGE,"E45");Q10=makeQuery(id+"F0.imprint","IMPRINT",FACE,{"disambiguationData":[TD([[makeQuery(id+"F0.imprint","IMPRINT",EDGE,{"derivedFrom":subQ3}),-1.0]])]});}
            var Q11;
            {var subQ3=sQuery(id+"F0.wireOp",EDGE,"E46");Q11=makeQuery(id+"F0.imprint","IMPRINT",FACE,{"disambiguationData":[TD([[makeQuery(id+"F0.imprint","IMPRINT",EDGE,{"derivedFrom":subQ3}),-1.0]])]});}
            var Q12;
            Q12=makeQuery(id+"F0.imprint","IMPRINT",FACE,{"disambiguationData":[TD([[makeQuery(id+"F0.imprint","IMPRINT",EDGE,{"derivedFrom":sQuery(id+"F0.wireOp",EDGE,"E45")}),1.0]])]});
            var Q13;
            {var subQ3=sQuery(id+"F0.wireOp",EDGE,"E64");Q13=makeQuery(id+"F0.imprint","IMPRINT",FACE,{"disambiguationData":[TD([[makeQuery(id+"F0.imprint","IMPRINT",EDGE,{"derivedFrom":subQ3}),1.0]])]});}
            var Q14;
            Q14=makeQuery(id+"F0.imprint","IMPRINT",FACE,{"disambiguationData":[TD([[makeQuery(id+"F0.imprint","IMPRINT",EDGE,{"derivedFrom":sQuery(id+"F0.wireOp",EDGE,"E63")}),-1.0]])]});
            var Q15;
            {var subQ3=sQuery(id+"F0.wireOp",EDGE,"E65");Q15=makeQuery(id+"F0.imprint","IMPRINT",FACE,{"disambiguationData":[TD([[makeQuery(id+"F0.imprint","IMPRINT",EDGE,{"derivedFrom":subQ3}),1.0]])]});}
            var Q16;
            {var subQ3=sQuery(id+"F0.wireOp",EDGE,"E63");Q16=makeQuery(id+"F0.imprint","IMPRINT",FACE,{"disambiguationData":[TD([[makeQuery(id+"F0.imprint","IMPRINT",EDGE,{"derivedFrom":subQ3}),1.0]])]});}
            var Q17;
            {var subQ3=sQuery(id+"F0.wireOp",EDGE,"E60");Q17=makeQuery(id+"F0.imprint","IMPRINT",FACE,{"disambiguationData":[TD([[makeQuery(id+"F0.imprint","IMPRINT",EDGE,{"derivedFrom":subQ3}),-1.0]])]});}
            var Q18;
            {var subQ0=sQuery(id+"F0.wireOp",EDGE,"E35");var subQ4=sQuery(id+"F0.wireOp",EDGE,"E33");var subQ7=makeQuery(id+"F0.imprint","INTERSECT",VERTEX,{"derivedFrom":[sQuery(id+"F0.wireOp",EDGE,"E8"),subQ4,subQ0]});Q18=makeQuery(id+"F0.imprint","IMPRINT",FACE,{"disambiguationData":[TD([[makeQuery(id+"F0.imprint","IMPRINT",EDGE,{"disambiguationData":[TD([[subQ7,-1.0]])],"derivedFrom":subQ4}),1.0]])]});}
            var Q19;
            {var subQ3=sQuery(id+"F0.wireOp",EDGE,"E66");Q19=makeQuery(id+"F0.imprint","IMPRINT",FACE,{"disambiguationData":[TD([[makeQuery(id+"F0.imprint","IMPRINT",EDGE,{"derivedFrom":subQ3}),1.0]])]});}
            var Q20;
            {var subQ3=sQuery(id+"F0.wireOp",EDGE,"E67");Q20=makeQuery(id+"F0.imprint","IMPRINT",FACE,{"disambiguationData":[TD([[makeQuery(id+"F0.imprint","IMPRINT",EDGE,{"derivedFrom":subQ3}),1.0]])]});}
            var Q21;
            Q21=makeQuery(id+"F0.imprint","IMPRINT",FACE,{"disambiguationData":[TD([[makeQuery(id+"F0.imprint","IMPRINT",EDGE,{"derivedFrom":sQuery(id+"F0.wireOp",EDGE,"E66")}),-1.0]])]});
            var Q22;
            {var subQ3=sQuery(id+"F0.wireOp",EDGE,"E68");Q22=makeQuery(id+"F0.imprint","IMPRINT",FACE,{"disambiguationData":[TD([[makeQuery(id+"F0.imprint","IMPRINT",EDGE,{"derivedFrom":subQ3}),1.0]])]});}
            var Q23;
            {var subQ3=sQuery(id+"F0.wireOp",EDGE,"E62");Q23=makeQuery(id+"F0.imprint","IMPRINT",FACE,{"disambiguationData":[TD([[makeQuery(id+"F0.imprint","IMPRINT",EDGE,{"derivedFrom":subQ3}),-1.0]])]});}
            var Q24;
            Q24=makeQuery(id+"F0.imprint","IMPRINT",FACE,{"disambiguationData":[TD([[makeQuery(id+"F0.imprint","IMPRINT",EDGE,{"derivedFrom":sQuery(id+"F0.wireOp",EDGE,"E60")}),1.0]])]});
            var Q25;
            {var subQ3=sQuery(id+"F0.wireOp",EDGE,"E61");Q25=makeQuery(id+"F0.imprint","IMPRINT",FACE,{"disambiguationData":[TD([[makeQuery(id+"F0.imprint","IMPRINT",EDGE,{"derivedFrom":subQ3}),-1.0]])]});}
            var Q26;
            {var subQ0=sQuery(id+"F0.wireOp",EDGE,"E8");var subQ3=sQuery(id+"F0.wireOp",EDGE,"E6");var subQ13=makeQuery(id+"F0.imprint","INTERSECT",VERTEX,{"derivedFrom":[sQuery(id+"F0.wireOp",EDGE,"E3"),subQ3,subQ0]});Q26=makeQuery(id+"F0.imprint","IMPRINT",FACE,{"disambiguationData":[TD([[makeQuery(id+"F0.imprint","IMPRINT",EDGE,{"disambiguationData":[TD([[subQ13,-1.0]])],"derivedFrom":subQ3}),-1.0]])]});}
            var Q27;
            {var subQ3=sQuery(id+"F0.wireOp",EDGE,"E52");Q27=makeQuery(id+"F0.imprint","IMPRINT",FACE,{"disambiguationData":[TD([[makeQuery(id+"F0.imprint","IMPRINT",EDGE,{"derivedFrom":subQ3}),1.0]])]});}
            var Q28;
            {var subQ3=sQuery(id+"F0.wireOp",EDGE,"E53");Q28=makeQuery(id+"F0.imprint","IMPRINT",FACE,{"disambiguationData":[TD([[makeQuery(id+"F0.imprint","IMPRINT",EDGE,{"derivedFrom":subQ3}),1.0]])]});}
            var Q29;
            {var subQ3=sQuery(id+"F0.wireOp",EDGE,"E51");Q29=makeQuery(id+"F0.imprint","IMPRINT",FACE,{"disambiguationData":[TD([[makeQuery(id+"F0.imprint","IMPRINT",EDGE,{"derivedFrom":subQ3}),1.0]])]});}
            var Q30;
            {var subQ3=sQuery(id+"F0.wireOp",EDGE,"E54");Q30=makeQuery(id+"F0.imprint","IMPRINT",FACE,{"disambiguationData":[TD([[makeQuery(id+"F0.imprint","IMPRINT",EDGE,{"derivedFrom":subQ3}),-1.0]])]});}
            var Q31;
            {var subQ3=sQuery(id+"F0.wireOp",EDGE,"E55");Q31=makeQuery(id+"F0.imprint","IMPRINT",FACE,{"disambiguationData":[TD([[makeQuery(id+"F0.imprint","IMPRINT",EDGE,{"derivedFrom":subQ3}),-1.0]])]});}
            var Q32;
            Q32=makeQuery(id+"F0.imprint","IMPRINT",FACE,{"disambiguationData":[TD([[makeQuery(id+"F0.imprint","IMPRINT",EDGE,{"derivedFrom":sQuery(id+"F0.wireOp",EDGE,"E51")}),-1.0]])]});
            var Q33;
            Q33=makeQuery(id+"F0.imprint","IMPRINT",FACE,{"disambiguationData":[TD([[makeQuery(id+"F0.imprint","IMPRINT",EDGE,{"derivedFrom":sQuery(id+"F0.wireOp",EDGE,"E54")}),1.0]])]});
            var Q34;
            {var subQ3=sQuery(id+"F0.wireOp",EDGE,"E56");Q34=makeQuery(id+"F0.imprint","IMPRINT",FACE,{"disambiguationData":[TD([[makeQuery(id+"F0.imprint","IMPRINT",EDGE,{"derivedFrom":subQ3}),-1.0]])]});}
            var Q35;
            {var subQ3=sQuery(id+"F0.wireOp",EDGE,"E59");Q35=makeQuery(id+"F0.imprint","IMPRINT",FACE,{"disambiguationData":[TD([[makeQuery(id+"F0.imprint","IMPRINT",EDGE,{"derivedFrom":subQ3}),1.0]])]});}
            var Q36;
            Q36=makeQuery(id+"F0.imprint","IMPRINT",FACE,{"disambiguationData":[TD([[makeQuery(id+"F0.imprint","IMPRINT",EDGE,{"derivedFrom":sQuery(id+"F0.wireOp",EDGE,"E57")}),-1.0]])]});
            var Q37;
            {var subQ3=sQuery(id+"F0.wireOp",EDGE,"E57");Q37=makeQuery(id+"F0.imprint","IMPRINT",FACE,{"disambiguationData":[TD([[makeQuery(id+"F0.imprint","IMPRINT",EDGE,{"derivedFrom":subQ3}),1.0]])]});}
            var Q38;
            {var subQ3=sQuery(id+"F0.wireOp",EDGE,"E58");Q38=makeQuery(id+"F0.imprint","IMPRINT",FACE,{"disambiguationData":[TD([[makeQuery(id+"F0.imprint","IMPRINT",EDGE,{"derivedFrom":subQ3}),1.0]])]});}
            var Q39;
            {var subQ0=sQuery(id+"F0.wireOp",EDGE,"E38");var subQ4=sQuery(id+"F0.wireOp",EDGE,"E36");var subQ7=makeQuery(id+"F0.imprint","INTERSECT",VERTEX,{"derivedFrom":[sQuery(id+"F0.wireOp",EDGE,"E6"),subQ4,subQ0]});Q39=makeQuery(id+"F0.imprint","IMPRINT",FACE,{"disambiguationData":[TD([[makeQuery(id+"F0.imprint","IMPRINT",EDGE,{"disambiguationData":[TD([[subQ7,-1.0]])],"derivedFrom":subQ4}),-1.0]])]});}
            var Q40;
            {var subQ3=sQuery(id+"F0.wireOp",EDGE,"E97");Q40=makeQuery(id+"F0.imprint","IMPRINT",FACE,{"disambiguationData":[TD([[makeQuery(id+"F0.imprint","IMPRINT",EDGE,{"derivedFrom":subQ3}),1.0]])]});}
            var Q41;
            Q41=makeQuery(id+"F0.imprint","IMPRINT",FACE,{"disambiguationData":[TD([[makeQuery(id+"F0.imprint","IMPRINT",EDGE,{"derivedFrom":sQuery(id+"F0.wireOp",EDGE,"E96")}),-1.0]])]});
            var Q42;
            {var subQ3=sQuery(id+"F0.wireOp",EDGE,"E98");Q42=makeQuery(id+"F0.imprint","IMPRINT",FACE,{"disambiguationData":[TD([[makeQuery(id+"F0.imprint","IMPRINT",EDGE,{"derivedFrom":subQ3}),1.0]])]});}
            var Q43;
            {var subQ3=sQuery(id+"F0.wireOp",EDGE,"E96");Q43=makeQuery(id+"F0.imprint","IMPRINT",FACE,{"disambiguationData":[TD([[makeQuery(id+"F0.imprint","IMPRINT",EDGE,{"derivedFrom":subQ3}),1.0]])]});}
            var Q44;
            {var subQ3=sQuery(id+"F0.wireOp",EDGE,"E99");Q44=makeQuery(id+"F0.imprint","IMPRINT",FACE,{"disambiguationData":[TD([[makeQuery(id+"F0.imprint","IMPRINT",EDGE,{"derivedFrom":subQ3}),-1.0]])]});}
            var Q45;
            {var subQ3=sQuery(id+"F0.wireOp",EDGE,"E101");Q45=makeQuery(id+"F0.imprint","IMPRINT",FACE,{"disambiguationData":[TD([[makeQuery(id+"F0.imprint","IMPRINT",EDGE,{"derivedFrom":subQ3}),-1.0]])]});}
            var Q46;
            {var subQ3=sQuery(id+"F0.wireOp",EDGE,"E100");Q46=makeQuery(id+"F0.imprint","IMPRINT",FACE,{"disambiguationData":[TD([[makeQuery(id+"F0.imprint","IMPRINT",EDGE,{"derivedFrom":subQ3}),-1.0]])]});}
            var Q47;
            {var subQ3=sQuery(id+"F0.wireOp",EDGE,"E102");Q47=makeQuery(id+"F0.imprint","IMPRINT",FACE,{"disambiguationData":[TD([[makeQuery(id+"F0.imprint","IMPRINT",EDGE,{"derivedFrom":subQ3}),1.0]])]});}
            var Q48;
            {var subQ3=sQuery(id+"F0.wireOp",EDGE,"E103");Q48=makeQuery(id+"F0.imprint","IMPRINT",FACE,{"disambiguationData":[TD([[makeQuery(id+"F0.imprint","IMPRINT",EDGE,{"derivedFrom":subQ3}),1.0]])]});}
            var Q49;
            {var subQ3=sQuery(id+"F0.wireOp",EDGE,"E104");Q49=makeQuery(id+"F0.imprint","IMPRINT",FACE,{"disambiguationData":[TD([[makeQuery(id+"F0.imprint","IMPRINT",EDGE,{"derivedFrom":subQ3}),1.0]])]});}
            var Q50;
            {var subQ0=sQuery(id+"F0.wireOp",EDGE,"E17");var subQ4=sQuery(id+"F0.wireOp",EDGE,"E15");var subQ7=makeQuery(id+"F0.imprint","INTERSECT",VERTEX,{"derivedFrom":[sQuery(id+"F0.wireOp",EDGE,"E9"),subQ4,subQ0]});Q50=makeQuery(id+"F0.imprint","IMPRINT",FACE,{"disambiguationData":[TD([[makeQuery(id+"F0.imprint","IMPRINT",EDGE,{"disambiguationData":[TD([[subQ7,-1.0]])],"derivedFrom":subQ4}),-1.0]])]});}
            var Q51;
            Q51=makeQuery(id+"F0.imprint","IMPRINT",FACE,{"disambiguationData":[TD([[makeQuery(id+"F0.imprint","IMPRINT",EDGE,{"derivedFrom":sQuery(id+"F0.wireOp",EDGE,"E102")}),-1.0]])]});
            var Q52;
            Q52=makeQuery(id+"F0.imprint","IMPRINT",FACE,{"disambiguationData":[TD([[makeQuery(id+"F0.imprint","IMPRINT",EDGE,{"derivedFrom":sQuery(id+"F0.wireOp",EDGE,"E99")}),1.0]])]});
            var Q53;
            {var subQ3=sQuery(id+"F0.wireOp",EDGE,"E106");Q53=makeQuery(id+"F0.imprint","IMPRINT",FACE,{"disambiguationData":[TD([[makeQuery(id+"F0.imprint","IMPRINT",EDGE,{"derivedFrom":subQ3}),1.0]])]});}
            var Q54;
            {var subQ3=sQuery(id+"F0.wireOp",EDGE,"E107");Q54=makeQuery(id+"F0.imprint","IMPRINT",FACE,{"disambiguationData":[TD([[makeQuery(id+"F0.imprint","IMPRINT",EDGE,{"derivedFrom":subQ3}),1.0]])]});}
            var Q55;
            {var subQ3=sQuery(id+"F0.wireOp",EDGE,"E105");Q55=makeQuery(id+"F0.imprint","IMPRINT",FACE,{"disambiguationData":[TD([[makeQuery(id+"F0.imprint","IMPRINT",EDGE,{"derivedFrom":subQ3}),1.0]])]});}
            var Q56;
            Q56=makeQuery(id+"F0.imprint","IMPRINT",FACE,{"disambiguationData":[TD([[makeQuery(id+"F0.imprint","IMPRINT",EDGE,{"derivedFrom":sQuery(id+"F0.wireOp",EDGE,"E105")}),-1.0]])]});
            var Q57;
            {var subQ3=sQuery(id+"F0.wireOp",EDGE,"E120");Q57=makeQuery(id+"F0.imprint","IMPRINT",FACE,{"disambiguationData":[TD([[makeQuery(id+"F0.imprint","IMPRINT",EDGE,{"derivedFrom":subQ3}),-1.0]])]});}
            var Q58;
            {var subQ3=sQuery(id+"F0.wireOp",EDGE,"E122");Q58=makeQuery(id+"F0.imprint","IMPRINT",FACE,{"disambiguationData":[TD([[makeQuery(id+"F0.imprint","IMPRINT",EDGE,{"derivedFrom":subQ3}),-1.0]])]});}
            var Q59;
            Q59=makeQuery(id+"F0.imprint","IMPRINT",FACE,{"disambiguationData":[TD([[makeQuery(id+"F0.imprint","IMPRINT",EDGE,{"derivedFrom":sQuery(id+"F0.wireOp",EDGE,"E120")}),1.0]])]});
            var Q60;
            {var subQ3=sQuery(id+"F0.wireOp",EDGE,"E121");Q60=makeQuery(id+"F0.imprint","IMPRINT",FACE,{"disambiguationData":[TD([[makeQuery(id+"F0.imprint","IMPRINT",EDGE,{"derivedFrom":subQ3}),-1.0]])]});}
            var Q61;
            {var subQ3=sQuery(id+"F0.wireOp",EDGE,"E114");Q61=makeQuery(id+"F0.imprint","IMPRINT",FACE,{"disambiguationData":[TD([[makeQuery(id+"F0.imprint","IMPRINT",EDGE,{"derivedFrom":subQ3}),1.0]])]});}
            var Q62;
            {var subQ3=sQuery(id+"F0.wireOp",EDGE,"E115");Q62=makeQuery(id+"F0.imprint","IMPRINT",FACE,{"disambiguationData":[TD([[makeQuery(id+"F0.imprint","IMPRINT",EDGE,{"derivedFrom":subQ3}),1.0]])]});}
            var Q63;
            {var subQ3=sQuery(id+"F0.wireOp",EDGE,"E116");Q63=makeQuery(id+"F0.imprint","IMPRINT",FACE,{"disambiguationData":[TD([[makeQuery(id+"F0.imprint","IMPRINT",EDGE,{"derivedFrom":subQ3}),1.0]])]});}
            var Q64;
            Q64=makeQuery(id+"F0.imprint","IMPRINT",FACE,{"disambiguationData":[TD([[makeQuery(id+"F0.imprint","IMPRINT",EDGE,{"derivedFrom":sQuery(id+"F0.wireOp",EDGE,"E114")}),-1.0]])]});
            var Q65;
            {var subQ1=sQuery(id+"F0.wireOp",EDGE,"E22");var subQ4=sQuery(id+"F0.wireOp",EDGE,"E21");var subQ5=makeQuery(id+"F0.imprint","INTERSECT",VERTEX,{"derivedFrom":[sQuery(id+"F0.wireOp",EDGE,"E14"),subQ4,subQ1]});Q65=makeQuery(id+"F0.imprint","IMPRINT",FACE,{"disambiguationData":[TD([[makeQuery(id+"F0.imprint","IMPRINT",EDGE,{"disambiguationData":[TD([[subQ5,-1.0]])],"derivedFrom":subQ4}),1.0]])]});}
            var Q66;
            {var subQ3=sQuery(id+"F0.wireOp",EDGE,"E109");Q66=makeQuery(id+"F0.imprint","IMPRINT",FACE,{"disambiguationData":[TD([[makeQuery(id+"F0.imprint","IMPRINT",EDGE,{"derivedFrom":subQ3}),1.0]])]});}
            var Q67;
            {var subQ3=sQuery(id+"F0.wireOp",EDGE,"E108");Q67=makeQuery(id+"F0.imprint","IMPRINT",FACE,{"disambiguationData":[TD([[makeQuery(id+"F0.imprint","IMPRINT",EDGE,{"derivedFrom":subQ3}),1.0]])]});}
            var Q68;
            {var subQ3=sQuery(id+"F0.wireOp",EDGE,"E110");Q68=makeQuery(id+"F0.imprint","IMPRINT",FACE,{"disambiguationData":[TD([[makeQuery(id+"F0.imprint","IMPRINT",EDGE,{"derivedFrom":subQ3}),1.0]])]});}
            var Q69;
            {var subQ3=sQuery(id+"F0.wireOp",EDGE,"E117");Q69=makeQuery(id+"F0.imprint","IMPRINT",FACE,{"disambiguationData":[TD([[makeQuery(id+"F0.imprint","IMPRINT",EDGE,{"derivedFrom":subQ3}),-1.0]])]});}
            var Q70;
            {var subQ3=sQuery(id+"F0.wireOp",EDGE,"E112");Q70=makeQuery(id+"F0.imprint","IMPRINT",FACE,{"disambiguationData":[TD([[makeQuery(id+"F0.imprint","IMPRINT",EDGE,{"derivedFrom":subQ3}),-1.0]])]});}
            var Q71;
            {var subQ3=sQuery(id+"F0.wireOp",EDGE,"E111");Q71=makeQuery(id+"F0.imprint","IMPRINT",FACE,{"disambiguationData":[TD([[makeQuery(id+"F0.imprint","IMPRINT",EDGE,{"derivedFrom":subQ3}),-1.0]])]});}
            var Q72;
            {var subQ3=sQuery(id+"F0.wireOp",EDGE,"E113");Q72=makeQuery(id+"F0.imprint","IMPRINT",FACE,{"disambiguationData":[TD([[makeQuery(id+"F0.imprint","IMPRINT",EDGE,{"derivedFrom":subQ3}),-1.0]])]});}
            var Q73;
            {var subQ3=sQuery(id+"F0.wireOp",EDGE,"E118");Q73=makeQuery(id+"F0.imprint","IMPRINT",FACE,{"disambiguationData":[TD([[makeQuery(id+"F0.imprint","IMPRINT",EDGE,{"derivedFrom":subQ3}),-1.0]])]});}
            var Q74;
            {var subQ3=sQuery(id+"F0.wireOp",EDGE,"E119");Q74=makeQuery(id+"F0.imprint","IMPRINT",FACE,{"disambiguationData":[TD([[makeQuery(id+"F0.imprint","IMPRINT",EDGE,{"derivedFrom":subQ3}),-1.0]])]});}
            var Q75;
            Q75=makeQuery(id+"F0.imprint","IMPRINT",FACE,{"disambiguationData":[TD([[makeQuery(id+"F0.imprint","IMPRINT",EDGE,{"derivedFrom":sQuery(id+"F0.wireOp",EDGE,"E117")}),1.0]])]});
            var Q76;
            {var subQ0=sQuery(id+"F0.wireOp",EDGE,"E20");var subQ4=sQuery(id+"F0.wireOp",EDGE,"E18");var subQ7=makeQuery(id+"F0.imprint","INTERSECT",VERTEX,{"derivedFrom":[sQuery(id+"F0.wireOp",EDGE,"E13"),subQ4,subQ0]});Q76=makeQuery(id+"F0.imprint","IMPRINT",FACE,{"disambiguationData":[TD([[makeQuery(id+"F0.imprint","IMPRINT",EDGE,{"disambiguationData":[TD([[subQ7,-1.0]])],"derivedFrom":subQ4}),1.0]])]});}
            var Q77;
            Q77=makeQuery(id+"F0.imprint","IMPRINT",FACE,{"disambiguationData":[TD([[makeQuery(id+"F0.imprint","IMPRINT",EDGE,{"derivedFrom":sQuery(id+"F0.wireOp",EDGE,"E111")}),1.0]])]});
            var Q78;
            Q78=makeQuery(id+"F0.imprint","IMPRINT",FACE,{"disambiguationData":[TD([[makeQuery(id+"F0.imprint","IMPRINT",EDGE,{"derivedFrom":sQuery(id+"F0.wireOp",EDGE,"E108")}),-1.0]])]});
            var Q79;
            {var subQ3=sQuery(id+"F0.wireOp",EDGE,"E13");var subQ7=sQuery(id+"F0.wireOp",EDGE,"E9");var subQ11=makeQuery(id+"F0.imprint","INTERSECT",VERTEX,{"derivedFrom":[sQuery(id+"F0.wireOp",EDGE,"E4"),subQ7,subQ3]});Q79=makeQuery(id+"F0.imprint","IMPRINT",FACE,{"disambiguationData":[TD([[makeQuery(id+"F0.imprint","IMPRINT",EDGE,{"disambiguationData":[TD([[subQ11,-1.0]])],"derivedFrom":subQ7}),1.0]])]});}
            var Q80;
            {var subQ3=sQuery(id+"F0.wireOp",EDGE,"E70");Q80=makeQuery(id+"F0.imprint","IMPRINT",FACE,{"disambiguationData":[TD([[makeQuery(id+"F0.imprint","IMPRINT",EDGE,{"derivedFrom":subQ3}),-1.0]])]});}
            var Q81;
            {var subQ3=sQuery(id+"F0.wireOp",EDGE,"E69");Q81=makeQuery(id+"F0.imprint","IMPRINT",FACE,{"disambiguationData":[TD([[makeQuery(id+"F0.imprint","IMPRINT",EDGE,{"derivedFrom":subQ3}),-1.0]])]});}
            var Q82;
            {var subQ3=sQuery(id+"F0.wireOp",EDGE,"E71");Q82=makeQuery(id+"F0.imprint","IMPRINT",FACE,{"disambiguationData":[TD([[makeQuery(id+"F0.imprint","IMPRINT",EDGE,{"derivedFrom":subQ3}),-1.0]])]});}
            var Q83;
            {var subQ3=sQuery(id+"F0.wireOp",EDGE,"E72");Q83=makeQuery(id+"F0.imprint","IMPRINT",FACE,{"disambiguationData":[TD([[makeQuery(id+"F0.imprint","IMPRINT",EDGE,{"derivedFrom":subQ3}),-1.0]])]});}
            var Q84;
            {var subQ3=sQuery(id+"F0.wireOp",EDGE,"E75");Q84=makeQuery(id+"F0.imprint","IMPRINT",FACE,{"disambiguationData":[TD([[makeQuery(id+"F0.imprint","IMPRINT",EDGE,{"derivedFrom":subQ3}),1.0]])]});}
            var Q85;
            {var subQ3=sQuery(id+"F0.wireOp",EDGE,"E76");Q85=makeQuery(id+"F0.imprint","IMPRINT",FACE,{"disambiguationData":[TD([[makeQuery(id+"F0.imprint","IMPRINT",EDGE,{"derivedFrom":subQ3}),1.0]])]});}
            var Q86;
            {var subQ3=sQuery(id+"F0.wireOp",EDGE,"E73");Q86=makeQuery(id+"F0.imprint","IMPRINT",FACE,{"disambiguationData":[TD([[makeQuery(id+"F0.imprint","IMPRINT",EDGE,{"derivedFrom":subQ3}),-1.0]])]});}
            var Q87;
            Q87=makeQuery(id+"F0.imprint","IMPRINT",FACE,{"disambiguationData":[TD([[makeQuery(id+"F0.imprint","IMPRINT",EDGE,{"derivedFrom":sQuery(id+"F0.wireOp",EDGE,"E69")}),1.0]])]});
            var Q88;
            Q88=makeQuery(id+"F0.imprint","IMPRINT",FACE,{"disambiguationData":[TD([[makeQuery(id+"F0.imprint","IMPRINT",EDGE,{"derivedFrom":sQuery(id+"F0.wireOp",EDGE,"E75")}),-1.0]])]});
            var Q89;
            {var subQ3=sQuery(id+"F0.wireOp",EDGE,"E77");Q89=makeQuery(id+"F0.imprint","IMPRINT",FACE,{"disambiguationData":[TD([[makeQuery(id+"F0.imprint","IMPRINT",EDGE,{"derivedFrom":subQ3}),1.0]])]});}
            var Q90;
            {var subQ3=sQuery(id+"F0.wireOp",EDGE,"E74");Q90=makeQuery(id+"F0.imprint","IMPRINT",FACE,{"disambiguationData":[TD([[makeQuery(id+"F0.imprint","IMPRINT",EDGE,{"derivedFrom":subQ3}),-1.0]])]});}
            var Q91;
            {var subQ0=sQuery(id+"F0.wireOp",EDGE,"E32");var subQ4=sQuery(id+"F0.wireOp",EDGE,"E30");var subQ7=makeQuery(id+"F0.imprint","INTERSECT",VERTEX,{"derivedFrom":[sQuery(id+"F0.wireOp",EDGE,"E10"),subQ4,subQ0]});Q91=makeQuery(id+"F0.imprint","IMPRINT",FACE,{"disambiguationData":[TD([[makeQuery(id+"F0.imprint","IMPRINT",EDGE,{"disambiguationData":[TD([[subQ7,-1.0]])],"derivedFrom":subQ4}),-1.0]])]});}
            var Q92;
            Q92=makeQuery(id+"F0.imprint","IMPRINT",FACE,{"disambiguationData":[TD([[makeQuery(id+"F0.imprint","IMPRINT",EDGE,{"derivedFrom":sQuery(id+"F0.wireOp",EDGE,"E72")}),1.0]])]});
            var Q93;
            {var subQ3=sQuery(id+"F0.wireOp",EDGE,"E79");Q93=makeQuery(id+"F0.imprint","IMPRINT",FACE,{"disambiguationData":[TD([[makeQuery(id+"F0.imprint","IMPRINT",EDGE,{"derivedFrom":subQ3}),1.0]])]});}
            var Q94;
            {var subQ3=sQuery(id+"F0.wireOp",EDGE,"E80");Q94=makeQuery(id+"F0.imprint","IMPRINT",FACE,{"disambiguationData":[TD([[makeQuery(id+"F0.imprint","IMPRINT",EDGE,{"derivedFrom":subQ3}),1.0]])]});}
            var Q95;
            {var subQ3=sQuery(id+"F0.wireOp",EDGE,"E83");Q95=makeQuery(id+"F0.imprint","IMPRINT",FACE,{"disambiguationData":[TD([[makeQuery(id+"F0.imprint","IMPRINT",EDGE,{"derivedFrom":subQ3}),1.0]])]});}
            var Q96;
            {var subQ3=sQuery(id+"F0.wireOp",EDGE,"E84");Q96=makeQuery(id+"F0.imprint","IMPRINT",FACE,{"disambiguationData":[TD([[makeQuery(id+"F0.imprint","IMPRINT",EDGE,{"derivedFrom":subQ3}),1.0]])]});}
            var Q97;
            {var subQ3=sQuery(id+"F0.wireOp",EDGE,"E82");Q97=makeQuery(id+"F0.imprint","IMPRINT",FACE,{"disambiguationData":[TD([[makeQuery(id+"F0.imprint","IMPRINT",EDGE,{"derivedFrom":subQ3}),1.0]])]});}
            var Q98;
            {var subQ3=sQuery(id+"F0.wireOp",EDGE,"E78");Q98=makeQuery(id+"F0.imprint","IMPRINT",FACE,{"disambiguationData":[TD([[makeQuery(id+"F0.imprint","IMPRINT",EDGE,{"derivedFrom":subQ3}),1.0]])]});}
            var Q99;
            {var subQ3=sQuery(id+"F0.wireOp",EDGE,"E85");Q99=makeQuery(id+"F0.imprint","IMPRINT",FACE,{"disambiguationData":[TD([[makeQuery(id+"F0.imprint","IMPRINT",EDGE,{"derivedFrom":subQ3}),-1.0]])]});}
            var Q100;
            {var subQ3=sQuery(id+"F0.wireOp",EDGE,"E86");Q100=makeQuery(id+"F0.imprint","IMPRINT",FACE,{"disambiguationData":[TD([[makeQuery(id+"F0.imprint","IMPRINT",EDGE,{"derivedFrom":subQ3}),-1.0]])]});}
            var Q101;
            {var subQ3=sQuery(id+"F0.wireOp",EDGE,"E87");Q101=makeQuery(id+"F0.imprint","IMPRINT",FACE,{"disambiguationData":[TD([[makeQuery(id+"F0.imprint","IMPRINT",EDGE,{"derivedFrom":subQ3}),-1.0]])]});}
            var Q102;
            Q102=makeQuery(id+"F0.imprint","IMPRINT",FACE,{"disambiguationData":[TD([[makeQuery(id+"F0.imprint","IMPRINT",EDGE,{"derivedFrom":sQuery(id+"F0.wireOp",EDGE,"E78")}),-1.0]])]});
            var Q103;
            {var subQ0=sQuery(id+"F0.wireOp",EDGE,"E26");var subQ4=sQuery(id+"F0.wireOp",EDGE,"E24");var subQ7=makeQuery(id+"F0.imprint","INTERSECT",VERTEX,{"derivedFrom":[sQuery(id+"F0.wireOp",EDGE,"E12"),subQ4,subQ0]});Q103=makeQuery(id+"F0.imprint","IMPRINT",FACE,{"disambiguationData":[TD([[makeQuery(id+"F0.imprint","IMPRINT",EDGE,{"disambiguationData":[TD([[subQ7,-1.0]])],"derivedFrom":subQ4}),-1.0]])]});}
            var Q104;
            Q104=makeQuery(id+"F0.imprint","IMPRINT",FACE,{"disambiguationData":[TD([[makeQuery(id+"F0.imprint","IMPRINT",EDGE,{"derivedFrom":sQuery(id+"F0.wireOp",EDGE,"E85")}),1.0]])]});
            var Q105;
            Q105=makeQuery(id+"F0.imprint","IMPRINT",FACE,{"disambiguationData":[TD([[makeQuery(id+"F0.imprint","IMPRINT",EDGE,{"derivedFrom":sQuery(id+"F0.wireOp",EDGE,"E82")}),-1.0]])]});
            var Q106;
            {var subQ3=sQuery(id+"F0.wireOp",EDGE,"E89");Q106=makeQuery(id+"F0.imprint","IMPRINT",FACE,{"disambiguationData":[TD([[makeQuery(id+"F0.imprint","IMPRINT",EDGE,{"derivedFrom":subQ3}),1.0]])]});}
            var Q107;
            {var subQ3=sQuery(id+"F0.wireOp",EDGE,"E88");Q107=makeQuery(id+"F0.imprint","IMPRINT",FACE,{"disambiguationData":[TD([[makeQuery(id+"F0.imprint","IMPRINT",EDGE,{"derivedFrom":subQ3}),1.0]])]});}
            var Q108;
            {var subQ3=sQuery(id+"F0.wireOp",EDGE,"E90");Q108=makeQuery(id+"F0.imprint","IMPRINT",FACE,{"disambiguationData":[TD([[makeQuery(id+"F0.imprint","IMPRINT",EDGE,{"derivedFrom":subQ3}),-1.0]])]});}
            var Q109;
            {var subQ3=sQuery(id+"F0.wireOp",EDGE,"E91");Q109=makeQuery(id+"F0.imprint","IMPRINT",FACE,{"disambiguationData":[TD([[makeQuery(id+"F0.imprint","IMPRINT",EDGE,{"derivedFrom":subQ3}),-1.0]])]});}
            var Q110;
            {var subQ3=sQuery(id+"F0.wireOp",EDGE,"E92");Q110=makeQuery(id+"F0.imprint","IMPRINT",FACE,{"disambiguationData":[TD([[makeQuery(id+"F0.imprint","IMPRINT",EDGE,{"derivedFrom":subQ3}),-1.0]])]});}
            var Q111;
            {var subQ3=sQuery(id+"F0.wireOp",EDGE,"E95");Q111=makeQuery(id+"F0.imprint","IMPRINT",FACE,{"disambiguationData":[TD([[makeQuery(id+"F0.imprint","IMPRINT",EDGE,{"derivedFrom":subQ3}),1.0]])]});}
            var Q112;
            {var subQ3=sQuery(id+"F0.wireOp",EDGE,"E94");Q112=makeQuery(id+"F0.imprint","IMPRINT",FACE,{"disambiguationData":[TD([[makeQuery(id+"F0.imprint","IMPRINT",EDGE,{"derivedFrom":subQ3}),1.0]])]});}
            var Q113;
            {var subQ3=sQuery(id+"F0.wireOp",EDGE,"E93");Q113=makeQuery(id+"F0.imprint","IMPRINT",FACE,{"disambiguationData":[TD([[makeQuery(id+"F0.imprint","IMPRINT",EDGE,{"derivedFrom":subQ3}),1.0]])]});}
            var Q114;
            {var subQ3=sQuery(id+"F0.wireOp",EDGE,"E81");Q114=makeQuery(id+"F0.imprint","IMPRINT",FACE,{"disambiguationData":[TD([[makeQuery(id+"F0.imprint","IMPRINT",EDGE,{"derivedFrom":subQ3}),-1.0]])]});}
            var Q115;
            Q115=makeQuery(id+"F0.imprint","IMPRINT",FACE,{"disambiguationData":[TD([[makeQuery(id+"F0.imprint","IMPRINT",EDGE,{"derivedFrom":sQuery(id+"F0.wireOp",EDGE,"E81")}),1.0]])]});
            var Q116;
            {var subQ0=sQuery(id+"F0.wireOp",EDGE,"E29");var subQ4=sQuery(id+"F0.wireOp",EDGE,"E27");var subQ7=makeQuery(id+"F0.imprint","INTERSECT",VERTEX,{"derivedFrom":[sQuery(id+"F0.wireOp",EDGE,"E11"),subQ4,subQ0]});Q116=makeQuery(id+"F0.imprint","IMPRINT",FACE,{"disambiguationData":[TD([[makeQuery(id+"F0.imprint","IMPRINT",EDGE,{"disambiguationData":[TD([[subQ7,-1.0]])],"derivedFrom":subQ4}),-1.0]])]});}
            var Q117;
            Q117=makeQuery(id+"F0.imprint","IMPRINT",FACE,{"disambiguationData":[TD([[makeQuery(id+"F0.imprint","IMPRINT",EDGE,{"derivedFrom":sQuery(id+"F0.wireOp",EDGE,"E90")}),1.0]])]});
            var Q118;
            Q118=makeQuery(id+"F0.imprint","IMPRINT",FACE,{"disambiguationData":[TD([[makeQuery(id+"F0.imprint","IMPRINT",EDGE,{"derivedFrom":sQuery(id+"F0.wireOp",EDGE,"E93")}),-1.0]])]});
            var Q119;
            {var subQ0=sQuery(id+"F0.wireOp",EDGE,"E12");var subQ4=sQuery(id+"F0.wireOp",EDGE,"E10");var subQ13=makeQuery(id+"F0.imprint","INTERSECT",VERTEX,{"derivedFrom":[sQuery(id+"F0.wireOp",EDGE,"E5"),subQ4,subQ0]});Q119=makeQuery(id+"F0.imprint","IMPRINT",FACE,{"disambiguationData":[TD([[makeQuery(id+"F0.imprint","IMPRINT",EDGE,{"disambiguationData":[TD([[subQ13,-1.0]])],"derivedFrom":subQ4}),-1.0]])]});}
            var Q120;
            {var subQ0=sQuery(id+"F0.wireOp",EDGE,"E5");var subQ11=sQuery(id+"F0.wireOp",EDGE,"E3");var subQ19=makeQuery(id+"F0.imprint","INTERSECT",VERTEX,{"derivedFrom":[sQuery(id+"F0.wireOp",EDGE,"E2"),subQ11,subQ0]});Q120=makeQuery(id+"F0.imprint","IMPRINT",FACE,{"disambiguationData":[TD([[makeQuery(id+"F0.imprint","IMPRINT",EDGE,{"disambiguationData":[TD([[subQ19,-1.0]])],"derivedFrom":subQ11}),1.0]])]});}
            extrude(context, id + "F2", {"entities" : qUnion([Q0, Q1, Q2, Q3, Q4, Q5, Q6, Q7, Q8, Q9, Q10, Q11, Q12, Q13, Q14, Q15, Q16, Q17, Q18, Q19, Q20, Q21, Q22, Q23, Q24, Q25, Q26, Q27, Q28, Q29, Q30, Q31, Q32, Q33, Q34, Q35, Q36, Q37, Q38, Q39, Q40, Q41, Q42, Q43, Q44, Q45, Q46, Q47, Q48, Q49, Q50, Q51, Q52, Q53, Q54, Q55, Q56, Q57, Q58, Q59, Q60, Q61, Q62, Q63, Q64, Q65, Q66, Q67, Q68, Q69, Q70, Q71, Q72, Q73, Q74, Q75, Q76, Q77, Q78, Q79, Q80, Q81, Q82, Q83, Q84, Q85, Q86, Q87, Q88, Q89, Q90, Q91, Q92, Q93, Q94, Q95, Q96, Q97, Q98, Q99, Q100, Q101, Q102, Q103, Q104, Q105, Q106, Q107, Q108, Q109, Q110, Q111, Q112, Q113, Q114, Q115, Q116, Q117, Q118, Q119, Q120]), "oppositeDirection" : true, "depth" : 3.8 * mm});
        }
    });
